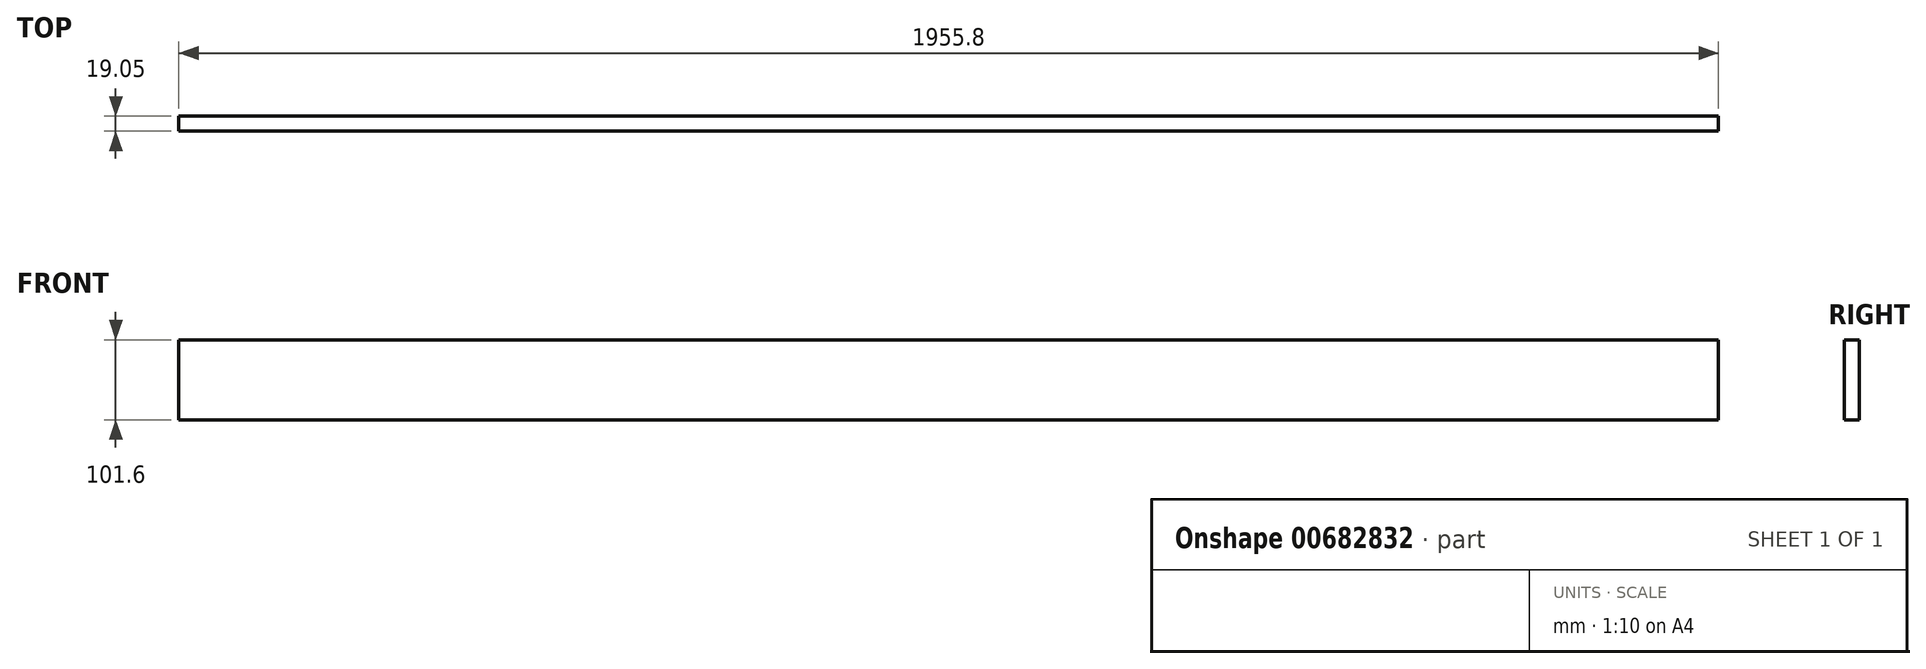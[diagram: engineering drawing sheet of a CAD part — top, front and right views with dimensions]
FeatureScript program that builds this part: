
annotation { "Feature Type Name" : "Feature", "Feature Type Description" : "" }
export const myFeature = defineFeature(function(context is Context, id is Id, definition is map)
    precondition{}
    {
        {
            var Q0;
            Q0=qCreatedBy(makeId("Front.planeOp"),FACE);
            var sketch = newSketch(context, id + "F0", { "sketchPlane" : qUnion([Q0])});
            skLineSegment(sketch, "E0.bottom", {"start": v(0, 0) * mm, "end": v(-1955.8, 0) * mm});
            skLineSegment(sketch, "E0.top", {"start": v(0, 101.6) * mm, "end": v(-1955.8, 101.6) * mm});
            skLineSegment(sketch, "E0.left", {"start": v(0, 0) * mm, "end": v(0, 101.6) * mm});
            skLineSegment(sketch, "E0.right", {"start": v(-1955.8, 0) * mm, "end": v(-1955.8, 101.6) * mm});
            skSolve(sketch);
        }
        {
            var Q0;
            Q0=qSketchRegion(id+"F0",true);
            extrude(context, id + "F1", {"entities" : qUnion([Q0]), "depth" : 19.05 * mm, "offsetDistance" : 25.4 * mm});
        }
    });
